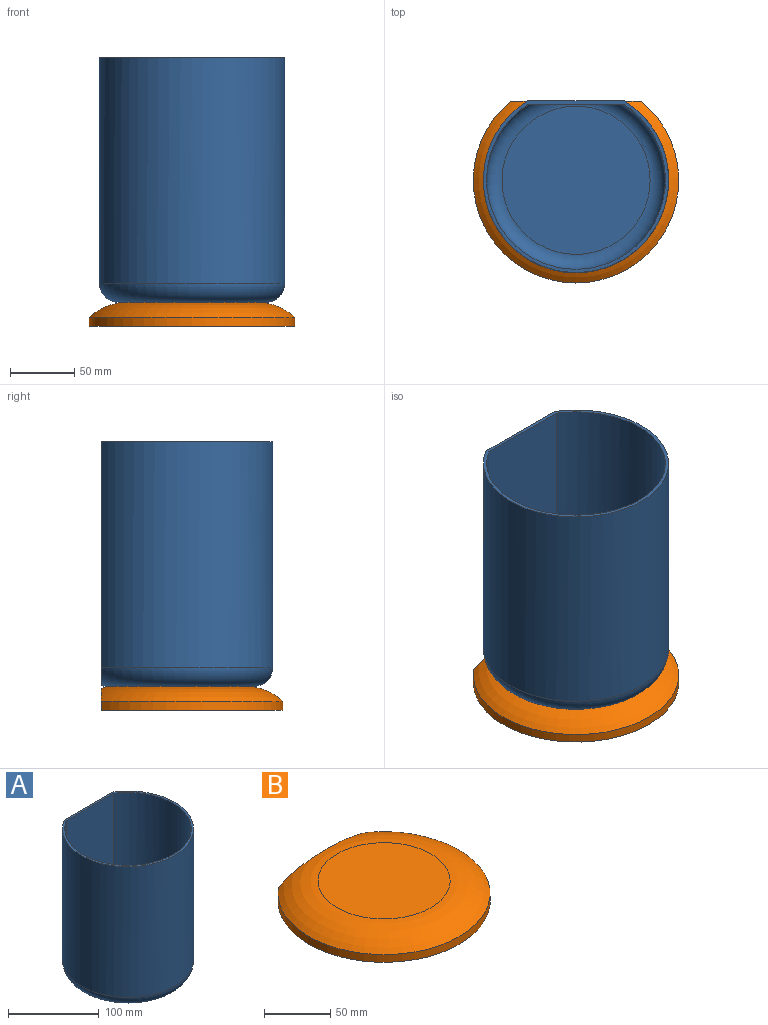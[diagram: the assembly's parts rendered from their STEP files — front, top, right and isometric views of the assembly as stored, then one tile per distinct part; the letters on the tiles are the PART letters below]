
ASSEMBLY  parts=2 mates=1
PART A: 9 faces, bbox 156.6x156.6x191 mm
  f0: cylinder r=72.34mm len=176.51mm, axis (0,0,-1), area 66162.6mm2, adj f1,f2,f4
  f1: plane 144.68x133.98mm, normal (0,0,1), area 1106.7mm2, adj f0,f4,f5,f8
  f2: torus R=57.85mm, axis (0,0,1), area 8454.2mm2, adj f0,f3,f4
  f3: plane 115.71x115.71mm, normal (0,0,-1), area 10515.4mm2, adj f2
  f4: plane 190.5x75.74mm, normal (0,1,0), area 14248.4mm2, adj f0,f1,f2
  f5: cylinder r=69.84mm len=176.51mm, axis (0,0,-1), area 63628.7mm2, adj f1,f6,f8
  f6: torus R=57.85mm, axis (0,0,1), area 6719.2mm2, adj f5,f7,f8
  f7: plane 115.71x115.71mm, normal (0,0,1), area 10515.4mm2, adj f6
  f8: plane 188.43x74.3mm, normal (0,-1,0), area 13869mm2, adj f1,f5,f6
PART B: 46 faces, bbox 177.7x177.7x18.8 mm
  f0: plane 160.44x141.86mm, normal (0,0,-1), area 5943.6mm2, adj f1,f6,f7,f8,f9,f10,f11,f13
  f1: cylinder r=80.22mm len=160.44mm, axis (0,0,-1), area 2804.2mm2, adj f0,f2,f45
  f2: torus R=49.98mm, axis (0,0,1), area 12160mm2, adj f1,f12,f45
  f3: torus R=49.98mm, axis (0,0,1), area 0.9mm2, adj f9,f11,f45
  f4: torus R=49.98mm, axis (0,0,1), area 0.9mm2, adj f6,f10,f45
  f5: torus R=49.98mm, axis (0,0,1), area 588.3mm2, adj f7,f8,f28,f41,f42,f45
  f6: cylinder r=15.5mm len=4.2mm, axis (0,0,-1), area 14.3mm2, adj f0,f4,f10,f45
  f7: cylinder r=15.5mm len=31mm, axis (0,0,-1), area 543.5mm2, adj f0,f5,f31,f36,f42,f45
  f8: cylinder r=15.5mm len=31mm, axis (0,0,-1), area 543.5mm2, adj f0,f5,f32,f37,f41,f45
  f9: cylinder r=15.5mm len=4.2mm, axis (0,0,-1), area 14.3mm2, adj f0,f3,f11,f45
  f10: cylinder r=72.22mm len=3.37mm, axis (0,0,-1), area 5.7mm2, adj f0,f4,f6,f45
  f11: cylinder r=72.22mm len=3.37mm, axis (0,0,-1), area 5.7mm2, adj f0,f3,f9,f45
  f12: plane 99.97x99.97mm, normal (0,0,1), area 7848.5mm2, adj f2
  f13: cylinder r=7.5mm len=15mm, axis (0,0,-1), area 329.9mm2, adj f0,f23
  f14: plane 5x5mm, normal (0,0,-1), area 19.6mm2, adj f23
  f15: cylinder r=7.5mm len=15mm, axis (0,0,-1), area 329.9mm2, adj f0,f24
  f16: plane 5x5mm, normal (0,0,-1), area 19.6mm2, adj f24
  f17: cylinder r=7.5mm len=15mm, axis (0,0,-1), area 329.9mm2, adj f0,f25
  f18: plane 5x5mm, normal (0,0,-1), area 19.6mm2, adj f25
  f19: cylinder r=7.5mm len=15mm, axis (0,0,-1), area 329.9mm2, adj f0,f26
  f20: plane 5x5mm, normal (0,0,-1), area 19.6mm2, adj f26
  f21: cylinder r=7.5mm len=15mm, axis (0,0,-1), area 329.9mm2, adj f0,f27
  f22: plane 5x5mm, normal (0,0,-1), area 19.6mm2, adj f27
  f23: torus R=2.5mm, axis (0,0,-1), area 280.4mm2, adj f13,f14
  f24: torus R=2.5mm, axis (0,0,-1), area 280.4mm2, adj f15,f16
  f25: torus R=2.5mm, axis (0,0,-1), area 280.4mm2, adj f17,f18
  f26: torus R=2.5mm, axis (0,0,-1), area 280.4mm2, adj f19,f20
  f27: torus R=2.5mm, axis (0,0,-1), area 280.4mm2, adj f21,f22
  f28: plane 99.97x98.46mm, normal (0,0,-1), area 7191.5mm2, adj f5,f29,f30,f31,f32,f40,f41,f42
  f29: torus R=49.98mm, axis (0,0,1), area 1210.8mm2, adj f28,f33,f38,f39,f40,f44
  f30: torus R=49.98mm, axis (0,0,1), area 1210.8mm2, adj f28,f33,f34,f35,f43,f44
  f31: torus R=49.98mm, axis (0,0,1), area 1210.8mm2, adj f7,f28,f34,f36,f42,f43
  f32: torus R=49.98mm, axis (0,0,1), area 1210.8mm2, adj f8,f28,f37,f39,f40,f41
  f33: cylinder r=15.5mm len=31mm, axis (0,0,-1), area 574.5mm2, adj f0,f29,f30,f35,f38,f44
  f34: cylinder r=15.5mm len=31mm, axis (0,0,-1), area 574.5mm2, adj f0,f30,f31,f35,f36,f43
  f35: cylinder r=72.22mm len=63.2mm, axis (0,0,-1), area 278.1mm2, adj f0,f30,f33,f34
  f36: cylinder r=72.22mm len=74.3mm, axis (0,0,-1), area 278.1mm2, adj f0,f7,f31,f34
  f37: cylinder r=72.22mm len=74.3mm, axis (0,0,-1), area 278.1mm2, adj f0,f8,f32,f39
  f38: cylinder r=72.22mm len=63.2mm, axis (0,0,-1), area 278.1mm2, adj f0,f29,f33,f39
  f39: cylinder r=15.5mm len=31mm, axis (0,0,-1), area 574.5mm2, adj f0,f29,f32,f37,f38,f40
  f40: torus R=2.5mm, axis (0,0,-1), area 198.3mm2, adj f28,f29,f32,f39
  f41: torus R=2.5mm, axis (0,0,-1), area 198.3mm2, adj f5,f8,f28,f32
  f42: torus R=2.5mm, axis (0,0,-1), area 198.3mm2, adj f5,f7,f28,f31
  f43: torus R=2.5mm, axis (0,0,-1), area 198.3mm2, adj f28,f30,f31,f34
  f44: torus R=2.5mm, axis (0,0,-1), area 198.3mm2, adj f28,f29,f30,f33
  f45: plane 102.73x17.25mm, normal (0,1,0), area 970.1mm2, adj f0,f1,f2,f3,f4,f5,f6,f7
PLACE A t=(0,0,-8)mm
PLACE B t=(0,0,-8)mm
MATE fastened A.f0 <-> B.f1  axis (0,0,-1) through (0,0,-8)mm
